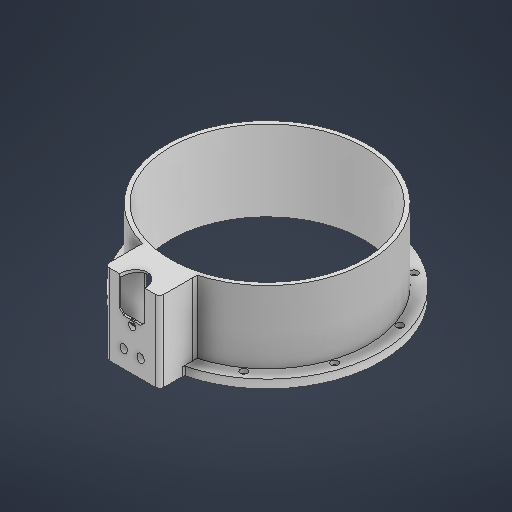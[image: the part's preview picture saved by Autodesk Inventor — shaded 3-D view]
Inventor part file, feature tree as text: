
AUTODESK INVENTOR PART (.ipt)
format: ipt  version: 2025 (Build 290162000, 162)  size: 629,760 bytes
history: native  units: in
note: dims shown in document units (in); Inventor stores cm internally (conversion verified against a paired STEP export)
features: extrude x23, sketch x20, fillet x4, other x3, plane x3, chamfer x2
ambient origin geometry x8: Origin, YZ Plane, XZ Plane, XY Plane, X Axis, Y Axis, Z Axis, Center Point
bodies: Body1 (feature_tree)
feature tree (55):
  other  "Cylinder.ipt"
  extrude  "Extrusion1"  Depth=0.3937in
  extrude  "Extrusion2"  Depth=0.3937in TaperAngle=0.0deg
  sketch  "Sketch3"  dims[d7=11.2205in d8=10.6299in]
  extrude  "Extrusion3"  Depth=10.6299in
  extrude  "Extrusion5"  Depth=0.1969in TaperAngle=0.0deg
  sketch  "Sketch6"  dims[d24=0.1969in d25=0.0in d31=0.0in d32=0.0in]
  extrude  "Extrusion6"  Depth=10.6299in
  extrude  "Extrusion7"  TaperAngle=0.0deg  [1 undecoded]
  extrude  "Extrusion8"  Depth=2.1654in
  plane  "Work Plane1"
  extrude  "Extrusion9"  Depth=9.065in
  extrude  "Extrusion21"  Depth=0.0787in
  sketch  "Sketch19"  dims[d107=2.2047in d108=0.0in d113=2.5591in]
  extrude  "Extrusion23"  Depth=2.5591in
  extrude  "Extrusion27"  Depth=0.0591in
  extrude  "Extrusion33"  Depth=0.5433in
  extrude  "Extrusion34"  Depth=0.0787in
  fillet  "Fillet10"  Radius=0.3937in
  fillet  "Fillet12"  Radius=1.5298in
  extrude  "Extrusion36"  Depth=0.0787in
  extrude  "Extrusion40"  Depth=4.1339in TaperAngle=0.0deg
  extrude  "Extrusion42"  Depth=0.0787in
  fillet  "Fillet19"  Radius=0.0787in
  fillet  "Fillet20"  Radius=0.1969in
  sketch  "Sketch30"  dims[d122=9.4488in d134=0.0787in d141=0.3937in d142=0.0in d164=1.5298in]
  sketch  "Sketch31"  dims[d165=0.0787in d166=1.8325in]
  extrude  "Extrusion44"  Depth=0.2165in
  chamfer  "Chamfer8"  Distance=3.937in Angle=360.0deg
  extrude  "Extrusion57"  Depth=9.065in
  extrude  "Extrusion58"  Depth=0.1181in
  plane  "Work Plane2"
  extrude  "Extrusion59"  Depth=0.1181in
  extrude  "Extrusion61"  Depth=0.1181in
  plane  "Work Plane3"
  extrude  "Extrusion63"  Depth=0.1181in
  chamfer  "Chamfer10"  Distance=2.7608in
  extrude  "Extrusion64"  Depth=0.1181in
  other  "Solid12::Cylinder.ipt"
  other  "TaggingFeature1"
  sketch  "Sketch1"  dims[d0=0.3937in d2=10.2362in]
  sketch  "Sketch2"  dims[d3=0.0in d4=0.0in d5=0.3937in d6=0.0in]
  sketch  "Sketch5"  dims[d17=10.6299in d18=0.2953in]
  sketch  "Sketch7"  dims[d33=2.1654in d34=0.0in d35=9.8425in]
  sketch  "Sketch9"  dims[d36=10.6299in d46=9.065in]
  sketch  "Sketch14"  dims[d47=0.3937in d48=0.0in d88=0.0787in]
  sketch  "Sketch22"  dims[d115=2.2047in d116=0.0in d117=0.0591in]
  sketch  "Sketch24"  dims[d119=0.5433in d120=0.5433in]
  sketch  "Sketch Circular Pattern3"  dims[d10=0.1969in d11=0.0in d15=0.1969in d16=0.0in]
  sketch  "Sketch45"  dims[d167=90.0deg d171=4.1339in d172=0.0in]
  sketch  "Sketch47"  dims[d173=1.1614in d174=0.0in d175=0.0787in d178=0.0787in d180=0.1969in]
  sketch  "Sketch48"  dims[d189=3.0541in d190=0.0in d209=0.2165in]
  sketch  "Sketch50"  dims[d210=0.3425in d211=3.937in d213=360.0deg]
  sketch  "Sketch52"  dims[d217=10.4151in d218=9.065in]
  sketch  "Sketch53"  dims[d221=0.3937in d222=0.0in d223=0.5433in d224=1.8228in d225=3.5433in d226=2.564in d227=2.7608in d228=3.5433in d233=1.9291in d234=0.0in d235=0.1969in d236=0.9916in d237=0.0in d238=0.1969in d246=2.1654in d247=0.0in d248=1.0787in d249=1.6412in d250=45.0deg d267=1.1811in d268=0.0787in d269=0.0787in d270=0.0787in d271=0.0443in d317=0.3346in d318=0.0in d319=0.0in d320=0.3346in d321=0.3346in d322=0.3937in d323=0.3937in d324=0.9055in d325=0.9055in d326=0.1575in d327=0.1575in d328=0.1575in d329=0.1575in d330=0.0in d331=0.8474in d334=0.9675in d335=0.0in d336=1.1811in d340=1.1778in d341=0.9675in d342=0.0in d346=3.3526in d347=1.4567in d348=0.5709in d349=1.1024in d350=0.0in d351=0.1969in d352=0.2037in d353=45.0deg d354=0.1969in d355=0.0394in d356=0.3937in d357=0.1181in d358=0.0in d359=0.187in d143=0.0197in d144=0.0344in d145=0.0197in d146=0.0344in d153=0.0in d154=0.0in d155=0.0in d156=0.0in d201=0.0197in d202=0.0344in d203=0.0197in d204=0.0344in d215=0.0197in d216=0.0344in d252=0.0197in d253=0.0344in d254=0.0197in d255=0.0344in d304=0.0197in d305=0.0344in d306=0.0197in d307=0.0344in]
note: 1 required parameter value undecoded (feature->parameter linkage not recoverable at this tier; creation-order binding heuristic only, values carry confidence <= 0.55)
